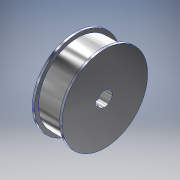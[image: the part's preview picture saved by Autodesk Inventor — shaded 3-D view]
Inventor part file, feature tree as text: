
AUTODESK INVENTOR PART (.ipt)
format: ipt  version: 2018 (Build 220112000, 112)  size: 137,216 bytes
history: native  units: mm
features: other x3, sketch x2, reference x2, revolve x1, extrude x1
ambient origin geometry x8: Origin, YZ Plane, XZ Plane, XY Plane, X Axis, Y Axis, Z Axis, Center Point
bodies: Solido1 (feature_tree)
feature tree (9):
  revolve  "Rivoluzione1"
  extrude  "Estrusione2"  Depth=7.0mm
  sketch  "Schizzo1"
  sketch  "Schizzo3"
  reference  "Riferimento1"
  reference  "Riferimento3"
  other  "Trasmissione cinghie - Taglio.iam"
  other  "Motorredutor Bonfiglioli :1"
  other  "MOTOR_C80_B5_X_X:1"
